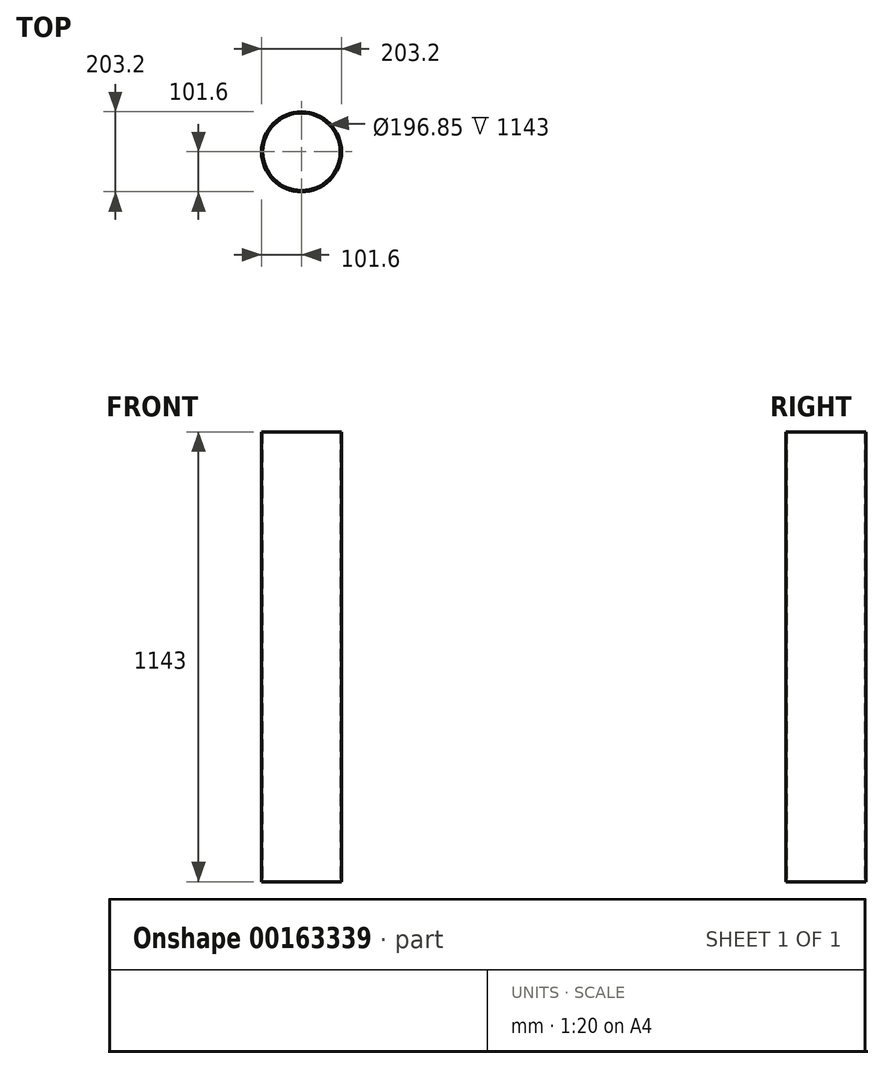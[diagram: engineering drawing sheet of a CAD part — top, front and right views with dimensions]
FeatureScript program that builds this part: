
annotation { "Feature Type Name" : "Feature", "Feature Type Description" : "" }
export const myFeature = defineFeature(function(context is Context, id is Id, definition is map)
    precondition{}
    {
        {
            var Q0;
            Q0=qCreatedBy(makeId("Top.planeOp"),FACE);
            var sketch = newSketch(context, id + "F0", { "sketchPlane" : qUnion([Q0])});
            skCircle(sketch, "E0", {"center": v(0, 0) * mm, "radius": 101.6 * mm});
            skCircle(sketch, "E1", {"center": v(0, 0) * mm, "radius": 98.43 * mm});
            skSolve(sketch);
        }
        {
            var Q0;
            Q0=makeQuery(id+"F0.imprint","IMPRINT",FACE,{"disambiguationData":[TD([[makeQuery(id+"F0.imprint","IMPRINT",EDGE,{"derivedFrom":sQuery(id+"F0.wireOp",EDGE,"E0")}),1.0]])]});
            extrude(context, id + "F1", {"entities" : qUnion([Q0]), "depth" : 1143 * mm});
        }
    });
